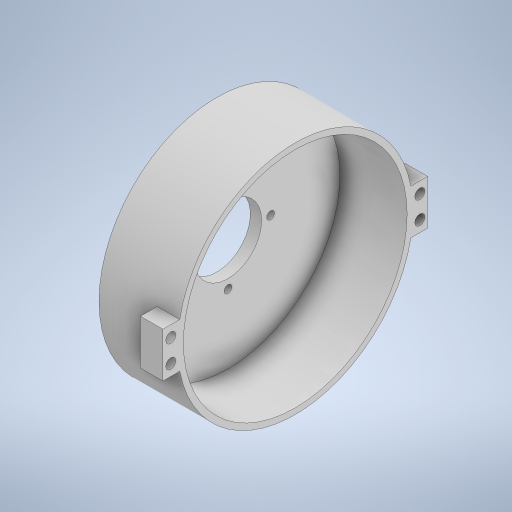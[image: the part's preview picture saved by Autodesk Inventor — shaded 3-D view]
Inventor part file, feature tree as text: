
AUTODESK INVENTOR PART (.ipt)
format: ipt  version: 2023 (Build 270158000, 158)  size: 331,264 bytes
history: native  units: mm
features: extrude x4, sketch x4
ambient origin geometry x8: Origin, YZ Plane, XZ Plane, XY Plane, X Axis, Y Axis, Z Axis, Center Point
bodies: Solid1 (feature_tree)
feature tree (8):
  extrude  "Extrusion1"  Depth=3.5mm
  extrude  "Extrusion2"  Depth=105.0mm
  extrude  "Extrusion3"  Depth=5.0mm TaperAngle=0.0deg
  extrude  "Extrusion4"  Depth=35.0mm TaperAngle=0.0deg
  sketch  "Sketch1"  dims[d0=38.0mm d1=3.5mm]
  sketch  "Sketch2"  dims[d2=40.0mm d4=360.0deg d6=105.0mm]
  sketch  "Sketch3"  dims[d7=80.0mm d8=5.0mm d9=0.0mm]
  sketch  "Sketch4"  dims[d10=105.0mm d11=35.0mm d12=0.0mm d14=10.0mm d15=20.0mm d17=5.0mm d18=4.5mm d19=5.0mm d20=4.5mm d21=20.0mm d23=360.0deg d25=10.0mm d26=0.0mm d27=30.0mm d28=10.0mm d29=45.0deg d30=10.0mm d31=10.0mm d32=0.0mm d33=105.0mm]
